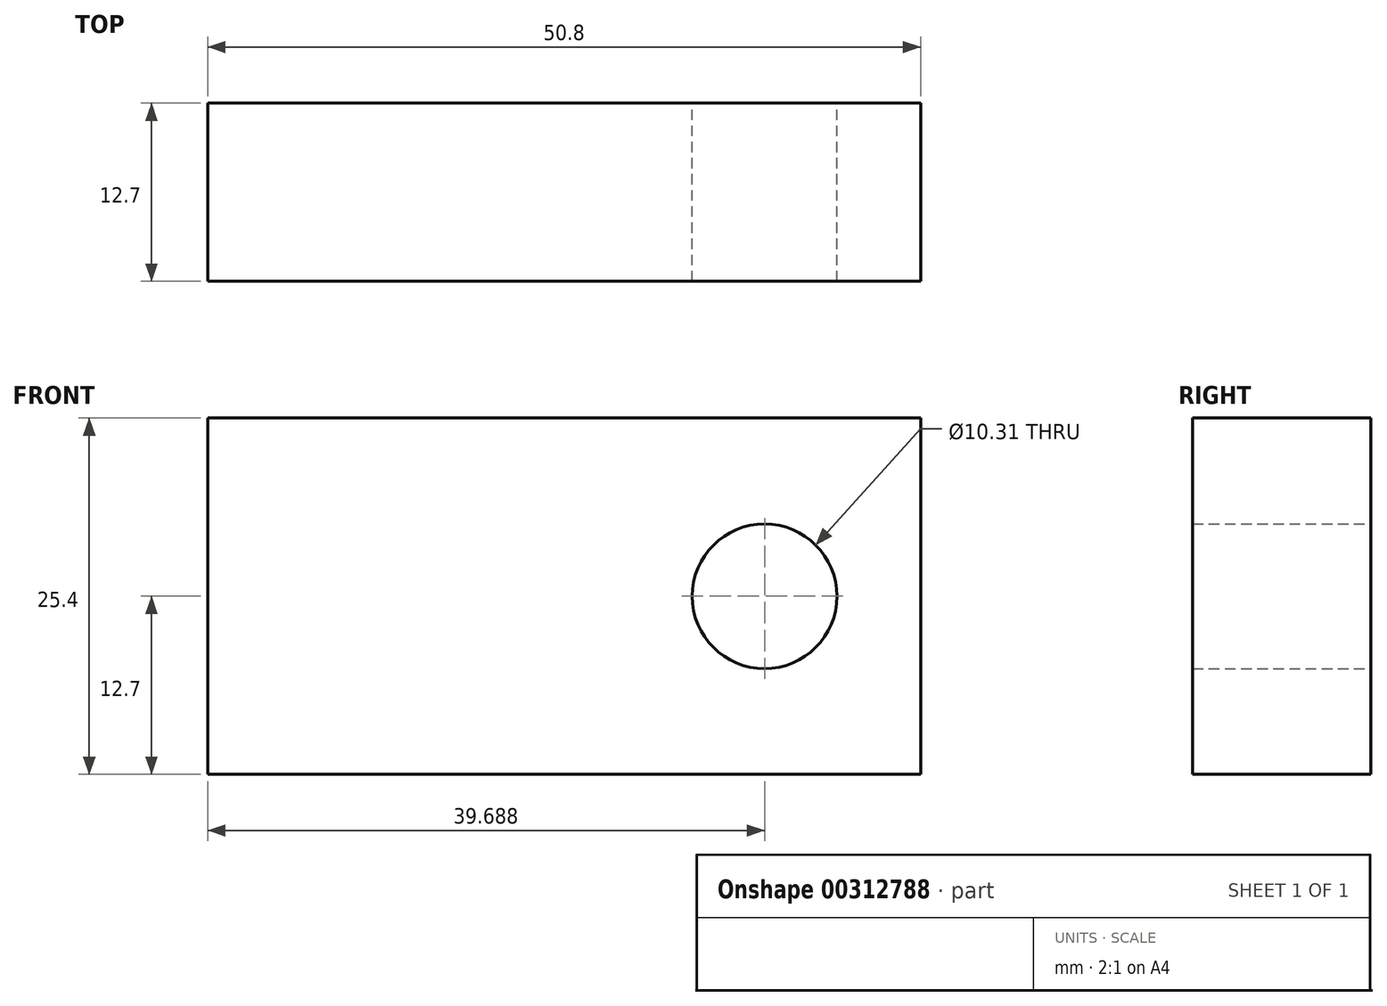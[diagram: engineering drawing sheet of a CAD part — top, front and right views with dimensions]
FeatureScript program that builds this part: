
annotation { "Feature Type Name" : "Feature", "Feature Type Description" : "" }
export const myFeature = defineFeature(function(context is Context, id is Id, definition is map)
    precondition{}
    {
        {
            var Q0;
            Q0=qCreatedBy(makeId("Front.planeOp"),FACE);
            var sketch = newSketch(context, id + "F0", { "sketchPlane" : qUnion([Q0])});
            skLineSegment(sketch, "E0.bottom", {"start": v(-25.4, 12.7) * mm, "end": v(25.4, 12.7) * mm});
            skLineSegment(sketch, "E0.top", {"start": v(-25.4, -12.7) * mm, "end": v(25.4, -12.7) * mm});
            skLineSegment(sketch, "E0.left", {"start": v(-25.4, 12.7) * mm, "end": v(-25.4, -12.7) * mm});
            skLineSegment(sketch, "E0.right", {"start": v(25.4, 12.7) * mm, "end": v(25.4, -12.7) * mm});
            skPoint(sketch, "E0.middle", {"position": v(0, 0) * mm});
            skCircle(sketch, "E1", {"center": v(14.29, 0) * mm, "radius": 5.16 * mm});
            skSolve(sketch);
        }
        {
            var Q0;
            Q0 = qSketchRegion(id + "F0", true);
            extrude(context, id + "F1", {"entities" : qUnion([Q0]), "endBound" : BoundingType.SYMMETRIC, "depth" : 12.7 * mm});
        }
    });
